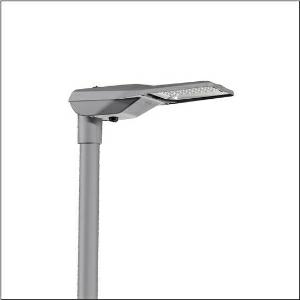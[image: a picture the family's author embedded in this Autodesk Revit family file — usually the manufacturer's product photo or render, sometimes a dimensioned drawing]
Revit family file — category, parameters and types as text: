
# Revit family: streetlight_sl_21_iq_mini___st0_5a_5xe2b31y08gb_b50d
name_source: partatom
category: Lighting Fixtures
units: mm (PartAtom-declared; Revit-internal decimal feet)

## family parameters
Cut with Voids When Loaded = No
Host = Face
Light Source = No
Part Type = Normal
Room Calculation Point = No
Round Connector Dimension = Use Diameter
Shared = No

## types (1)
- --- (1 x LED, 5990 lm, 39.8 W, 3000K)
    Apparent Load = 40 VA
    CIE Flux Codes = 41 75 97 100 100
    Color Rendering = 70
    Color Temperature = 3000K
    Default Elevation = 1800 mm
    Description = Streetlight SL 21 iQ mini, mast luminaire, primary light control with lens, of PMMA, primary optical cover: cover, of toughened safety glass, transparent, light distribution: ST0.5a, light emission: direct distribution, primary light characteristic: asymmetric, installation type: post-top, side-entry, LED, High Power LED, rated luminous flux: 5.990lm, luminous efficacy: 151lm/W, light colour: 730, colour temperature: 3000K, control gear: iQ-Street Remote, D4i with power reduction, control: pre-setting: logarithmic dimming characteristic, Street-Remote, Auto-Match, Temp-Guard, Lumen-Switch, Night-Set, Smart-Wire, Light-Fading, Desk-Remote (wireless, voltage-free reading and setting of iQ features in the workshop via application-optimized NFC function/RFID function), optimised constant luminous flux control (CLO 2.0), mains connection: 220..240V, AC, 50/60Hz, start of lifetime: 40W, end of service life: 41W, reduction: 18W, luminaire housing, of diecast aluminium, powder-coated, SITECO metallic grey (DB 702S), corrosivity category C5 high according to DIN EN ISO 12944, please order mast flange separately, inclination adjustable: 0°, 5°, 10°, 15°, sealing non-destructively replaceable, multi-level sealing system, length: 628mm, width: 235mm, height: 110mm, mast flange for spigot size: 42mm (side-entry): 5XC10008XM4, 60/48mm (side-entry/post-top): 5XC10108XM2, 76/60mm (side-entry/post-top): 5XC10108XM1, mounting height: 4..8m, Smart Interface below and above, protection rating (complete): IP66, insulation class (complete): insulation class II (safety insulation), certification: CE, ENEC, ENEC+, VDE, impact resistance: IK10, permissible operating ambient temperature for outdoor applications: -40..+50°C, standard-compliant lighting for roads and squares, packaging unit: 1 piece

Light Distribution: ST0.5a
    Height = 110 mm
    Lamp = 1 x LED
    Lamp Light Flux = 5990 lm
    Lamp Power = 39.8 W
    Lamp count = 1
    Length = 625 mm
    Luminous efficacy = 151 lm/W
    Manufacturer = Siteco
    ModVariant = No
    Model = 5XE2B31Y08GB
    Number of Poles = 1
    OnlyDefault = Yes
    Power Factor = 1
    Product Name = Streetlight SL 21 iQ mini | ST0.5a
    Product group = mast luminaire | pylon top
    ProductGroupID = 6100
    Protection Class = Protection class II
    Protection Degree = IP 66
    RLX_Detail_Level = 1
    RLX_Emergency_Light_Flux = 0 lm
    RLX_Emergency_Type = 0
    RLX_Emergency_Type_DB = No
    RlxData = <blob elided: 103965 chars, md5=944faca1>
    Socket = socket
    Standby Power = 0 W
    System Light Flux = 5990 lm
    System Power = 40 W
    Type Comments = factory setting: luminous flux: 100 % | dim-lin: 254 | 800 mA
    Type Image = l_1003514.jpg
    URL = http://relux.com
    VarID = @adj_116265
    Voltage = 0 V
    Weight = 0.00 kg
    Width = 234 mm

## geometry (parser evidence)
native form markers: Blend x4, Sweep x12
no freeform markers — native parametric forms only
